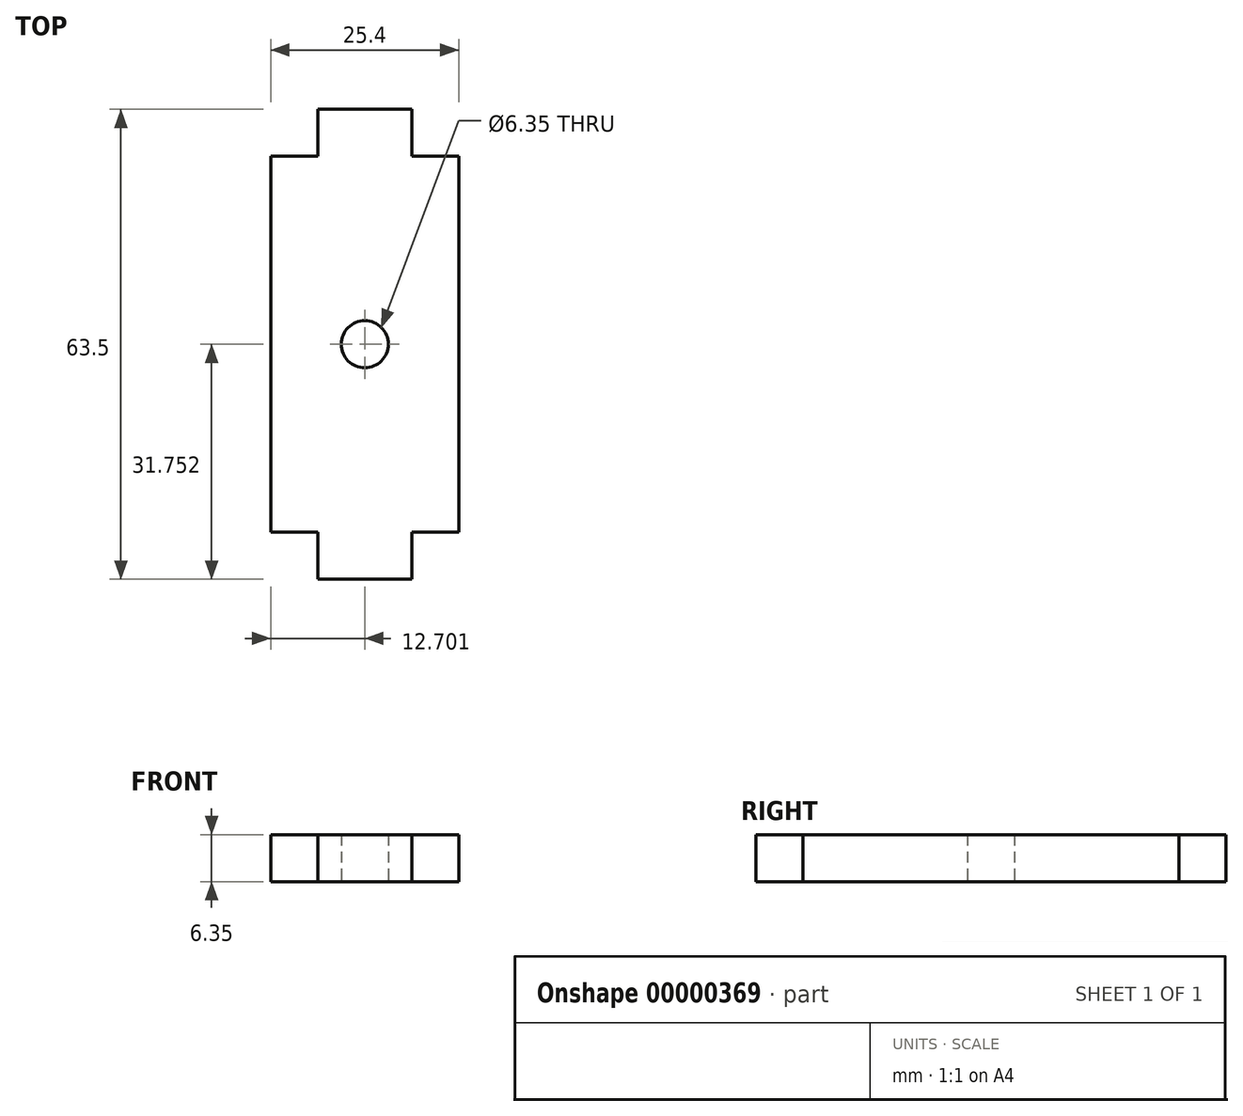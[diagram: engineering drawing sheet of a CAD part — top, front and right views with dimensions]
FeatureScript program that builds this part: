
annotation { "Feature Type Name" : "Feature", "Feature Type Description" : "" }
export const myFeature = defineFeature(function(context is Context, id is Id, definition is map)
    precondition{}
    {
        {
            var Q0;
            Q0=qCreatedBy(makeId("Top.planeOp"),FACE);
            var sketch = newSketch(context, id + "F0", { "sketchPlane" : qUnion([Q0])});
            skLineSegment(sketch, "E0.bottom", {"start": v(4, 14.13) * mm, "end": v(16.7, 14.13) * mm});
            skLineSegment(sketch, "E0.top", {"start": v(4, -49.37) * mm, "end": v(16.7, -49.37) * mm});
            skLineSegment(sketch, "E0.left", {"start": v(-2.35, 7.78) * mm, "end": v(-2.35, -43.02) * mm});
            skLineSegment(sketch, "E0.right", {"start": v(23.05, 7.78) * mm, "end": v(23.05, -43.02) * mm});
            skLineSegment(sketch, "E1", {"start": v(4, 14.13) * mm, "end": v(4, 7.78) * mm});
            skLineSegment(sketch, "E2", {"start": v(4, 7.78) * mm, "end": v(-2.35, 7.78) * mm});
            skLineSegment(sketch, "E3", {"start": v(16.7, 14.13) * mm, "end": v(16.7, 7.78) * mm});
            skLineSegment(sketch, "E4", {"start": v(16.7, 7.78) * mm, "end": v(23.05, 7.78) * mm});
            skLineSegment(sketch, "E5", {"start": v(-2.35, -43.02) * mm, "end": v(4, -43.02) * mm});
            skLineSegment(sketch, "E6", {"start": v(4, -43.02) * mm, "end": v(4, -49.37) * mm});
            skLineSegment(sketch, "E7", {"start": v(23.05, -43.02) * mm, "end": v(16.7, -43.02) * mm});
            skLineSegment(sketch, "E8", {"start": v(16.7, -43.02) * mm, "end": v(16.7, -49.37) * mm});
            skCircle(sketch, "E9", {"center": v(10.35, -17.62) * mm, "radius": 3.18 * mm});
            skCircle(sketch, "E10", {"center": v(10.35, -17.62) * mm, "radius": 26.18 * mm, "construction": true});
            skSolve(sketch);
        }
        {
            var Q0;
            Q0=makeQuery(id+"F0.imprint","IMPRINT",FACE,{"disambiguationData":[TD([[makeQuery(id+"F0.imprint","IMPRINT",EDGE,{"derivedFrom":sQuery(id+"F0.wireOp",EDGE,"E0.bottom")}),-1.0]])]});
            extrude(context, id + "F1", {"entities" : qUnion([Q0]), "depth" : 6.35 * mm});
        }
    });
